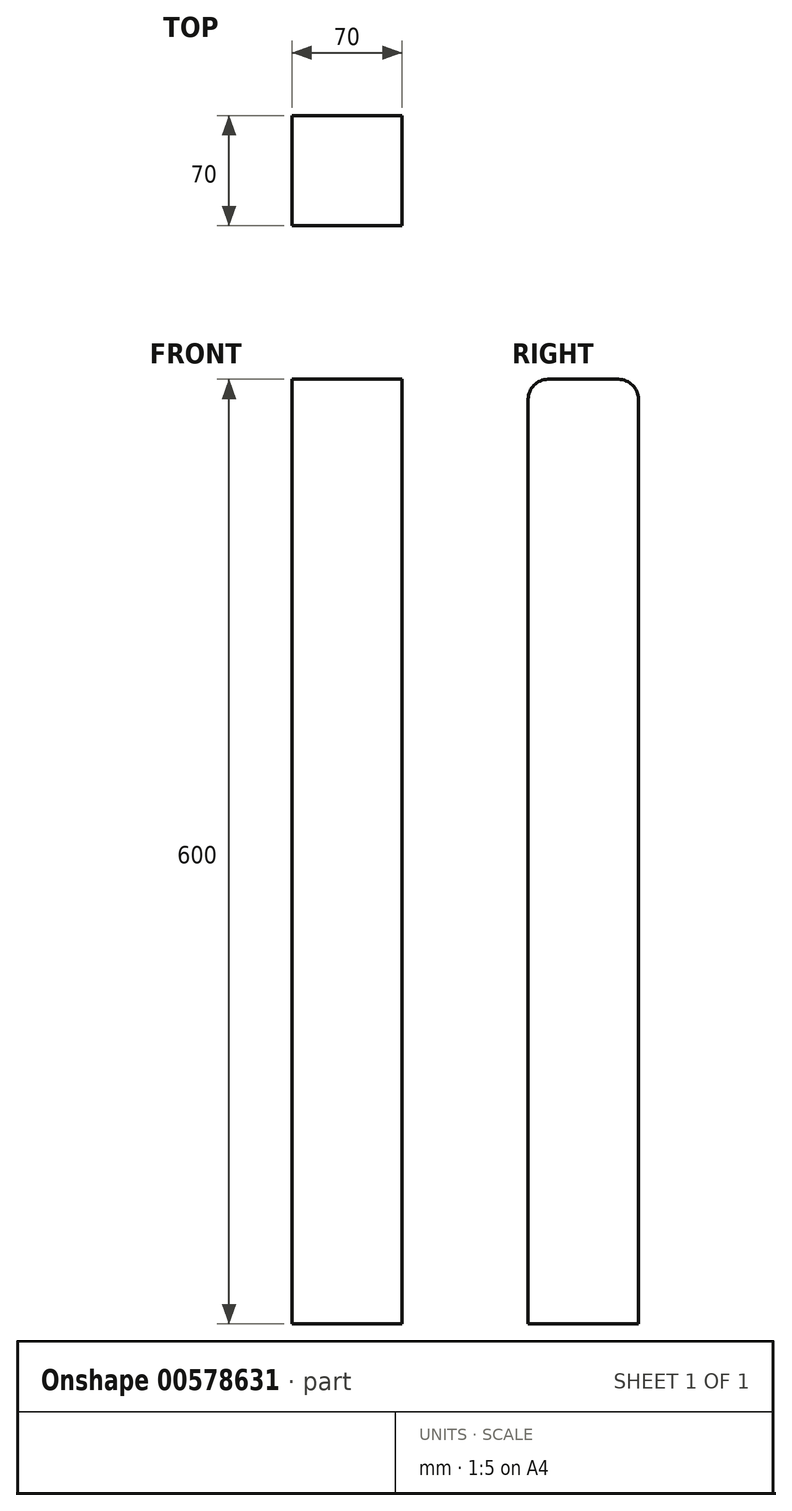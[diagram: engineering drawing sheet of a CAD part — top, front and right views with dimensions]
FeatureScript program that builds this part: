
annotation { "Feature Type Name" : "Feature", "Feature Type Description" : "" }
export const myFeature = defineFeature(function(context is Context, id is Id, definition is map)
    precondition{}
    {
        {
            var Q0;
            Q0=qCreatedBy(makeId("Front.planeOp"),FACE);
            var sketch = newSketch(context, id + "F0", { "sketchPlane" : qUnion([Q0])});
            skLineSegment(sketch, "E0.bottom", {"start": v(-35, 300) * mm, "end": v(35, 300) * mm});
            skLineSegment(sketch, "E0.top", {"start": v(-35, -300) * mm, "end": v(35, -300) * mm});
            skLineSegment(sketch, "E0.left", {"start": v(-35, 300) * mm, "end": v(-35, -300) * mm});
            skLineSegment(sketch, "E0.right", {"start": v(35, 300) * mm, "end": v(35, -300) * mm});
            skPoint(sketch, "E0.middle", {"position": v(0, 0) * mm});
            skSolve(sketch);
        }
        {
            var Q0;
            Q0=makeQuery(id+"F0.imprint","IMPRINT",FACE,{"disambiguationData":[TD([[makeQuery(id+"F0.imprint","IMPRINT",EDGE,{"derivedFrom":sQuery(id+"F0.wireOp",EDGE,"E0.bottom")}),-1.0]])]});
            extrude(context, id + "F1", {"entities" : qUnion([Q0]), "endBound" : BoundingType.SYMMETRIC, "depth" : 70 * mm, "offsetDistance" : 25.4 * mm});
        }
        {
            var Q0;
            Q0=makeQuery(id+"F1.opExtrude","CAP_EDGE",EDGE,{"disambiguationData":[OSD([sQuery(id+"F0.wireOp",EDGE,"E0.bottom")])],"isStart":false});
            var Q1;
            Q1=makeQuery(id+"F1.opExtrude","CAP_EDGE",EDGE,{"disambiguationData":[OSD([sQuery(id+"F0.wireOp",EDGE,"E0.bottom")])],"isStart":true});
            fillet(context, id + "F2", {"entities" : qUnion([Q0, Q1]), "radius" : 12.7 * mm, "tangentPropagation" : true, "allowEdgeOverflow" : false});
        }
    });
